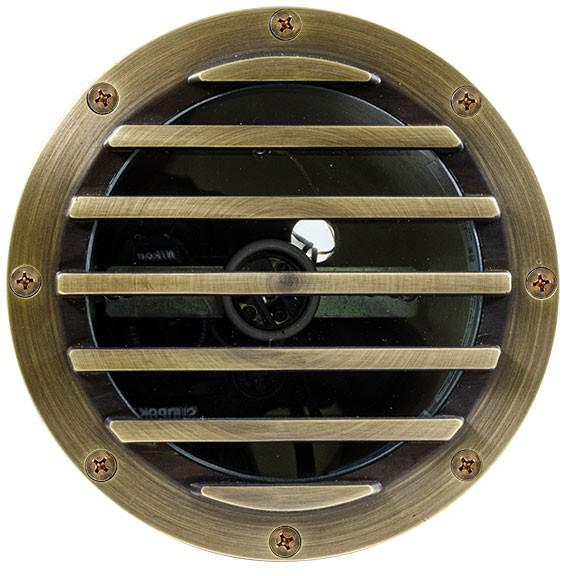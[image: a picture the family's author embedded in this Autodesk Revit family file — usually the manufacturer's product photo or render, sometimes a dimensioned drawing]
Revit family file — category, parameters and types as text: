
# Revit family: Alcon-9150-D90-Revit-Family
name_source: partatom
category: Luminarias
units: mm (PartAtom-declared; Revit-internal decimal feet)

## family parameters
Anfitrión = Cara
Compartido = No
Corte con vacíos al cargar = No
Cota de conector redondo = Usar diámetro
Mantener orientación de anotación = No
Origen de luz = Sí
Punto de cálculo de habitación = No
Tipo de pieza = Normal

## types (1)
- Alcon-9150-D90-Revit-Family
    Cambio de temperatura de color de luz atenuada = <Ninguno>
    Elevación por defecto = 4' - 0"
    Fabricante = Alcon Lighting
    Filtro de color = 16777215
    GLASS LENS = Analytical Panels
    HOUSING = <Por categoría>
    LENS GLASS = Glass
    Link to IES File = https://www.alconlighting.com
    Longitud de símbolo de origen de luz = 10' - 0"
    Modelo = Alcon Lighting 9150-D90
    Product Data URL = https://www.alconlighting.com
    Product Page = https://www.alconlighting.com
    TAP LENS = <Por categoría>
    TOP FINISH = <Por categoría>
    URL = https://www.alconlighting.com
    Ángulo de campo de foco = 90.00°
    Ángulo de enfoque = 30.00°
    Ángulo de inclinación = 60.00°

## geometry (parser evidence)
native form markers: Sweep x3
no freeform markers — native parametric forms only
